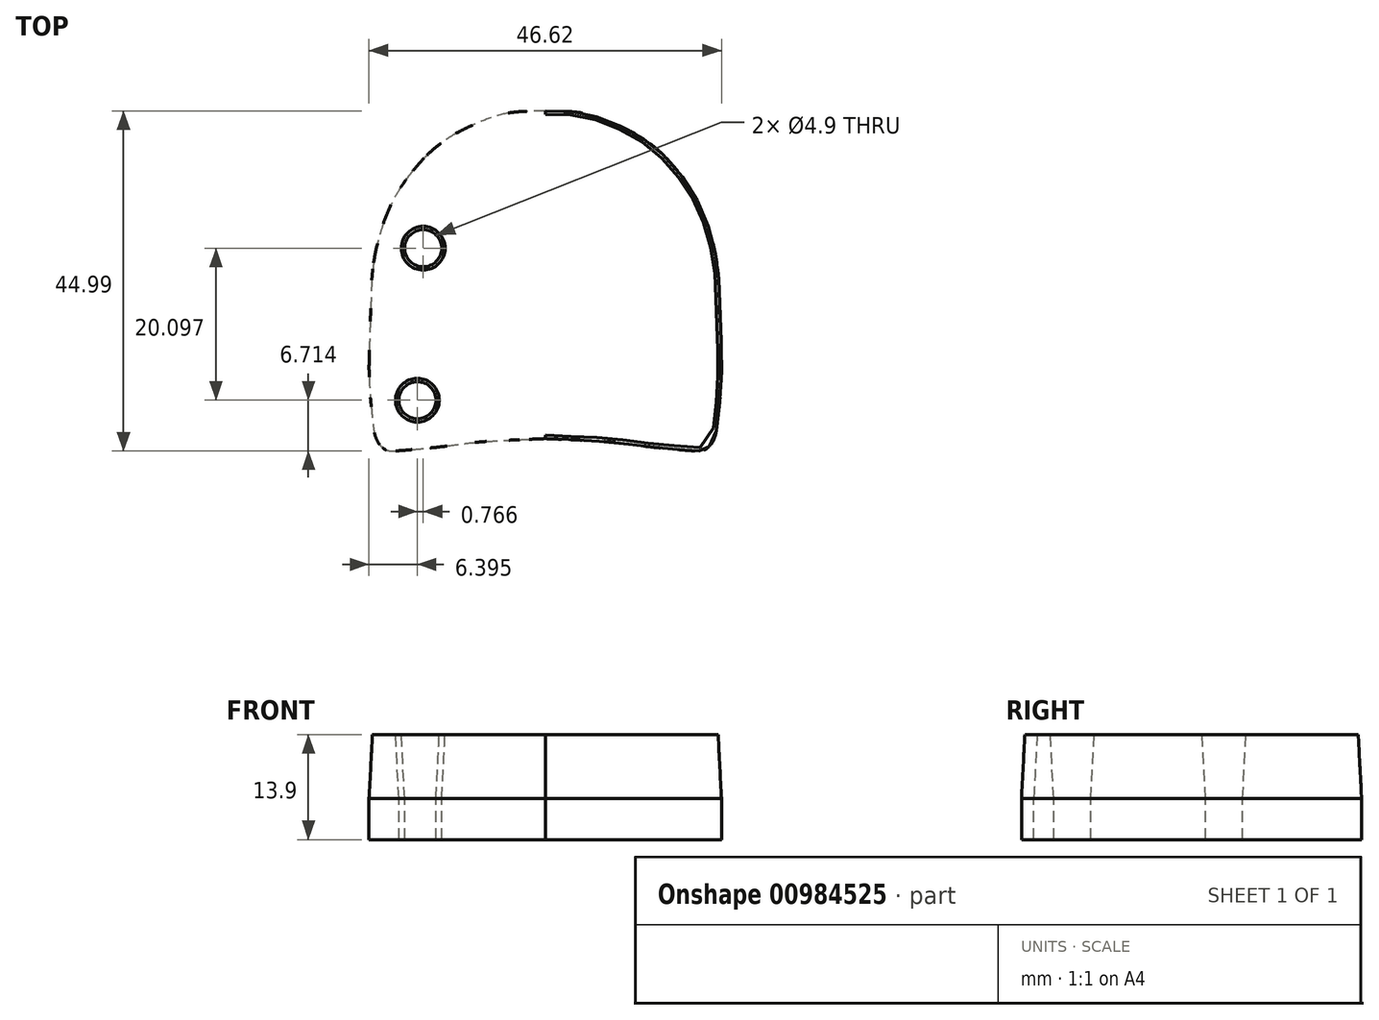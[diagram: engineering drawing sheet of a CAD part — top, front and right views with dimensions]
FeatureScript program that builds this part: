
annotation { "Feature Type Name" : "Feature", "Feature Type Description" : "" }
export const myFeature = defineFeature(function(context is Context, id is Id, definition is map)
    precondition{}
    {
        {
            var Q0;
            Q0=qCreatedBy(makeId("Top.planeOp"),FACE);
            var sketch = newSketch(context, id + "F0", { "sketchPlane" : qUnion([Q0])});
            skLineSegment(sketch, "E0", {"start": v(0, 26.02) * mm, "end": v(0, -17.34) * mm, "construction": true});
            skFitSpline(sketch, "E1", {"points": [v(0, 26.02) * mm, v(4.19, 25.83) * mm, v(8.06, 24.79) * mm, v(11.93, 22.96) * mm, v(14.97, 20.79) * mm, v(18.35, 17) * mm, v(20.72, 12.91) * mm, v(22.28, 8.11) * mm, v(22.9, 4.1) * mm, v(23.08, 0) * mm, v(23.3, -8.97) * mm, v(22.97, -13.61) * mm, v(22.47, -17.04) * mm, v(21.65, -18.43) * mm, v(21.03, -18.84) * mm, v(20.2, -18.97) * mm, v(17.07, -18.74) * mm, v(13.42, -18.37) * mm, v(9.4, -17.85) * mm, v(3.46, -17.49) * mm, v(0, -17.34) * mm], "startDerivative": vector(75.1, -5.18) * mm, "endDerivative": vector(-65.86, 2.89) * mm});
            skFitSpline(sketch, "E2.MirrorCS", {"points": [v(0, 26.02) * mm, v(-4.19, 25.83) * mm, v(-8.06, 24.79) * mm, v(-11.93, 22.96) * mm, v(-14.97, 20.79) * mm, v(-18.35, 17) * mm, v(-20.72, 12.91) * mm, v(-22.28, 8.11) * mm, v(-22.9, 4.1) * mm, v(-23.08, 0) * mm, v(-23.3, -8.97) * mm, v(-22.97, -13.61) * mm, v(-22.47, -17.04) * mm, v(-21.65, -18.43) * mm, v(-21.03, -18.84) * mm, v(-20.2, -18.97) * mm, v(-17.07, -18.74) * mm, v(-13.42, -18.37) * mm, v(-9.4, -17.85) * mm, v(-3.46, -17.49) * mm, v(0, -17.34) * mm], "startDerivative": vector(-75.1, -5.18) * mm, "endDerivative": vector(65.86, 2.89) * mm});
            skCircle(sketch, "E3", {"center": v(0, 20.01) * mm, "radius": 2.45 * mm});
            skCircle(sketch, "E4", {"center": v(16.15, 7.84) * mm, "radius": 2.45 * mm});
            skCircle(sketch, "E5", {"center": v(16.92, -12.26) * mm, "radius": 2.45 * mm});
            skCircle(sketch, "E6.MirrorC", {"center": v(-16.15, 7.84) * mm, "radius": 2.45 * mm});
            skCircle(sketch, "E7.MirrorC", {"center": v(-16.92, -12.26) * mm, "radius": 2.45 * mm});
            skSolve(sketch);
        }
        {
            var Q0;
            Q0=makeQuery(id+"F0.imprint","IMPRINT",FACE,{"disambiguationData":[TD([[makeQuery(id+"F0.imprint","IMPRINT",EDGE,{"derivedFrom":sQuery(id+"F0.wireOp",EDGE,"E1")}),-1.0]])]});
            var Q1;
            Q1=makeQuery(id+"F0.imprint","IMPRINT",FACE,{"disambiguationData":[TD([[makeQuery(id+"F0.imprint","IMPRINT",EDGE,{"derivedFrom":sQuery(id+"F0.wireOp",EDGE,"E4")}),1.0]])]});
            var Q2;
            Q2=makeQuery(id+"F0.imprint","IMPRINT",FACE,{"disambiguationData":[TD([[makeQuery(id+"F0.imprint","IMPRINT",EDGE,{"derivedFrom":sQuery(id+"F0.wireOp",EDGE,"E3")}),1.0]])]});
            var Q3;
            Q3=makeQuery(id+"F0.imprint","IMPRINT",FACE,{"disambiguationData":[TD([[makeQuery(id+"F0.imprint","IMPRINT",EDGE,{"derivedFrom":sQuery(id+"F0.wireOp",EDGE,"E5")}),1.0]])]});
            var Q4;
            Q4=makeQuery(id+"F0.imprint","IMPRINT",FACE,{"disambiguationData":[TD([[makeQuery(id+"F0.imprint","IMPRINT",EDGE,{"derivedFrom":sQuery(id+"F0.wireOp",EDGE,"E6.MirrorC")}),-1.0]])]});
            var Q5;
            Q5=makeQuery(id+"F0.imprint","IMPRINT",FACE,{"disambiguationData":[TD([[makeQuery(id+"F0.imprint","IMPRINT",EDGE,{"derivedFrom":sQuery(id+"F0.wireOp",EDGE,"E7.MirrorC")}),-1.0]])]});
            extrude(context, id + "F1", {"entities" : qUnion([Q0, Q1, Q2, Q3, Q4, Q5]), "oppositeDirection" : true, "depth" : 5.4 * mm, "offsetDistance" : 25 * mm});
        }
        {
            var Q0;
            Q0=makeQuery(id+"F0.imprint","IMPRINT",FACE,{"disambiguationData":[TD([[makeQuery(id+"F0.imprint","IMPRINT",EDGE,{"derivedFrom":sQuery(id+"F0.wireOp",EDGE,"E3")}),1.0]])]});
            var Q1;
            Q1=makeQuery(id+"F0.imprint","IMPRINT",FACE,{"disambiguationData":[TD([[makeQuery(id+"F0.imprint","IMPRINT",EDGE,{"derivedFrom":sQuery(id+"F0.wireOp",EDGE,"E6.MirrorC")}),-1.0]])]});
            var Q2;
            Q2=makeQuery(id+"F0.imprint","IMPRINT",FACE,{"disambiguationData":[TD([[makeQuery(id+"F0.imprint","IMPRINT",EDGE,{"derivedFrom":sQuery(id+"F0.wireOp",EDGE,"E7.MirrorC")}),-1.0]])]});
            var Q3;
            Q3=makeQuery(id+"F0.imprint","IMPRINT",FACE,{"disambiguationData":[TD([[makeQuery(id+"F0.imprint","IMPRINT",EDGE,{"derivedFrom":sQuery(id+"F0.wireOp",EDGE,"E5")}),1.0]])]});
            var Q4;
            Q4=makeQuery(id+"F0.imprint","IMPRINT",FACE,{"disambiguationData":[TD([[makeQuery(id+"F0.imprint","IMPRINT",EDGE,{"derivedFrom":sQuery(id+"F0.wireOp",EDGE,"E4")}),1.0]])]});
            extrude(context, id + "F2", {"entities" : qUnion([Q0, Q1, Q2, Q3, Q4]), "operationType" : NewBodyOperationType.ADD, "depth" : 8.5 * mm, "offsetDistance" : 25 * mm, "hasDraft" : true, "draftAngle" : 3 * degree, "draftPullDirection" : true});
        }
        {
            var Q0;
            Q0=makeQuery(id+"F2.opExtrude","CAP_EDGE",EDGE,{"disambiguationData":[OSD([sQuery(id+"F0.wireOp",EDGE,"E3")])],"isStart":true});
            var Q1;
            Q1=makeQuery(id+"F2.opExtrude","CAP_EDGE",EDGE,{"disambiguationData":[OSD([sQuery(id+"F0.wireOp",EDGE,"E6.MirrorC")])],"isStart":true});
            var Q2;
            Q2=makeQuery(id+"F2.opExtrude","CAP_EDGE",EDGE,{"disambiguationData":[OSD([sQuery(id+"F0.wireOp",EDGE,"E7.MirrorC")])],"isStart":true});
            var Q3;
            Q3=makeQuery(id+"F2.opExtrude","CAP_EDGE",EDGE,{"disambiguationData":[OSD([sQuery(id+"F0.wireOp",EDGE,"E5")])],"isStart":true});
            var Q4;
            Q4=makeQuery(id+"F2.opExtrude","CAP_EDGE",EDGE,{"disambiguationData":[OSD([sQuery(id+"F0.wireOp",EDGE,"E4")])],"isStart":true});
            fillet(context, id + "F3", {"entities" : qUnion([Q0, Q1, Q2, Q3, Q4]), "radius" : 1 * mm, "tangentPropagation" : true, "allowEdgeOverflow" : false});
        }
    });
